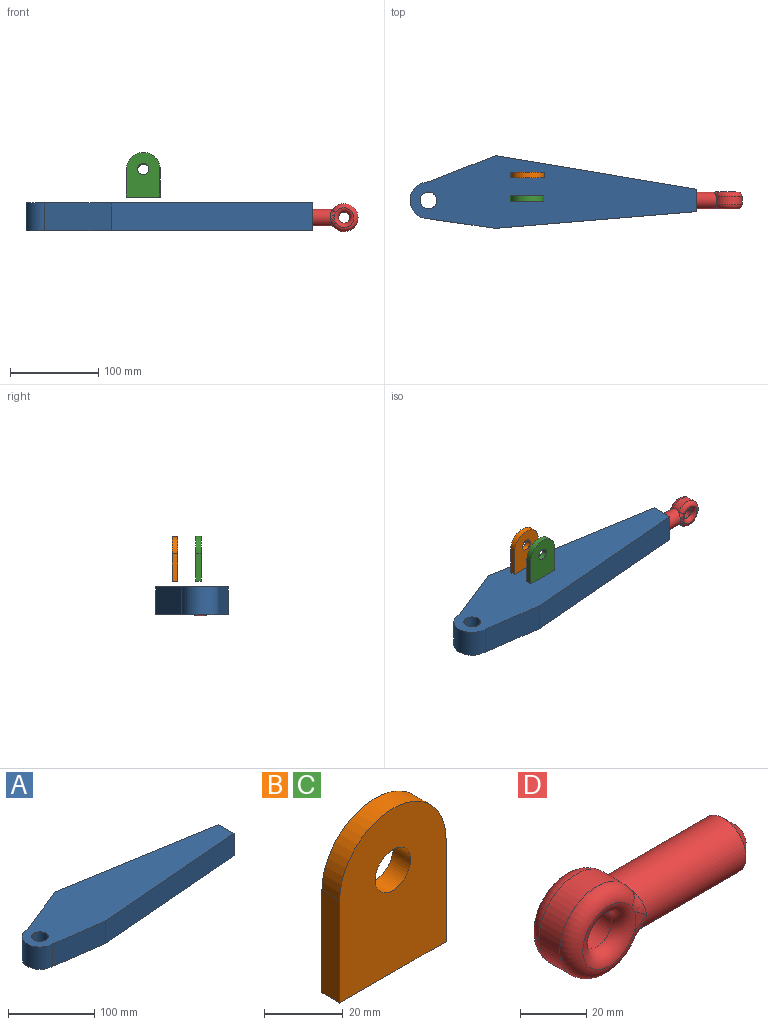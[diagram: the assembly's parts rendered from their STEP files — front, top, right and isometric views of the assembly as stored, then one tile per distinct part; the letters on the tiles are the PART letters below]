
ASSEMBLY  parts=4 mates=2
PART A: 11 faces, bbox 325.8x82.6x31.8 mm
  f0: cylinder r=20.96mm len=41.91mm, axis (0,0,-1), area 2090.2mm2, adj f1,f5,f7,f8
  f1: plane 75.92x31.75mm, normal (-0.14,-0.99,0), area 2434.8mm2, adj f0,f2,f7,f8
  f2: plane 228.88x31.75mm, normal (0.08,-1,0), area 7292mm2, adj f1,f3,f7,f8
  f3: plane 31.75x25.4mm, normal (1,0,0), area 521.4mm2, adj f2,f4,f7,f8,f9
  f4: plane 228.88x38.1mm, normal (0.16,0.99,0), area 7366.8mm2, adj f3,f5,f7,f8
  f5: plane 75.92x31.75mm, normal (-0.37,0.93,0), area 2590.1mm2, adj f0,f4,f7,f8
  f6: cylinder r=9.53mm len=31.75mm, axis (0,0,-1), area 1900.2mm2, adj f7,f8
  f7: plane 325.76x82.55mm, normal (0,0,1), area 17483.1mm2, adj f0,f1,f2,f3,f4,f5,f6
  f8: plane 325.76x82.55mm, normal (0,0,-1), area 17483.1mm2, adj f0,f1,f2,f3,f4,f5,f6
  f9: cylinder r=9.53mm len=25.4mm, axis (1,0,0), area 1520.1mm2, adj f3,f10
  f10: cone r=0mm half-angle=59deg, axis (1,0,0), area 332.5mm2, adj f9
PART B: 7 faces, bbox 38.1x6.4x50.8 mm
  f0: plane 31.75x6.35mm, normal (1,0,0), area 201.6mm2, adj f1,f3,f5,f6
  f1: cylinder r=19.05mm len=38.1mm, axis (0,1,0), area 380mm2, adj f0,f2,f5,f6
  f2: plane 31.75x6.35mm, normal (-1,0,0), area 201.6mm2, adj f1,f3,f5,f6
  f3: plane 38.1x6.35mm, normal (0,0,-1), area 241.9mm2, adj f0,f2,f5,f6
  f4: cylinder r=6.35mm len=12.7mm, axis (0,1,0), area 253.4mm2, adj f5,f6
  f5: plane 50.8x38.1mm, normal (0,-1,0), area 1653mm2, adj f0,f1,f2,f3,f4
  f6: plane 50.8x38.1mm, normal (0,1,0), area 1653mm2, adj f0,f1,f2,f3,f4
PART C: same geometry as B
PART D: 15 faces, bbox 81.4x19.8x35 mm
  f0: cylinder r=15.88mm len=31.75mm, axis (0,1,0), area 717mm2, adj f5,f7,f11
  f1: plane 8.89x8.89mm, normal (1,0,0), area 62.1mm2, adj f14
  f2: cylinder r=6.35mm len=12.7mm, axis (0,1,0), area 354.7mm2, adj f9,f13
  f3: plane 8.37x5.79mm, normal (0,-1,0), area 16.3mm2, adj f10,f12,f13
  f4: plane 8.37x5.79mm, normal (0,1,0), area 16.3mm2, adj f6,f8,f9
  f5: cylinder r=9.53mm len=45.72mm, axis (1,0,0), area 2648mm2, adj f0,f6,f8,f10,f12,f14
  f6: bspline ~8.61x6.93mm, area 30.4mm2, adj f4,f5,f7,f9
  f7: torus R=10.79mm, axis (0,-1,0), area 560.2mm2, adj f0,f6,f8,f9
  f8: bspline ~8.8x7.14mm, area 31.8mm2, adj f4,f5,f7,f9
  f9: torus R=11.43mm, axis (0,-1,0), area 391.7mm2, adj f2,f4,f6,f7,f8
  f10: bspline ~8.61x6.93mm, area 30.4mm2, adj f3,f5,f11,f13
  f11: torus R=10.79mm, axis (0,-1,0), area 560.2mm2, adj f0,f10,f12,f13
  f12: bspline ~8.8x7.14mm, area 31.5mm2, adj f3,f5,f11,f13
  f13: torus R=11.43mm, axis (0,-1,0), area 391.7mm2, adj f2,f3,f10,f11,f12
  f14: cone r=4.45mm half-angle=45deg, axis (-1,0,0), area 315.3mm2, adj f1,f5
PLACE A t=(-65.55,10.18,-2.47)mm
PLACE B t=(46.98,42.2,67.04)mm
PLACE C t=(46.67,15.57,67.64)mm
PLACE D rot(axis=(0,1,0),180deg) t=(274.82,19.71,12.52)mm
MATE slider C.f3 <-> A.f7  axis (0,0,1) through (65.72,15.57,35.89)mm
MATE slider D.f5 <-> A.f9  axis (-1,0,0) through (239.4,10.18,12.52)mm
